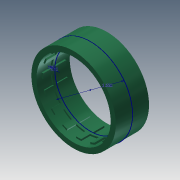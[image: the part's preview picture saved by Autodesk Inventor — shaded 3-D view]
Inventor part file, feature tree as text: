
AUTODESK INVENTOR PART (.ipt)
format: ipt  version: 2015 (Build 190159000, 159)  size: 231,424 bytes
history: native  units: in
note: dims shown in document units (in); Inventor stores cm internally (conversion verified against a paired STEP export)
features: extrude x3, sketch x2, plane x1, pattern_circular x1
ambient origin geometry x8: Origin, YZ Plane, XZ Plane, XY Plane, X Axis, Y Axis, Z Axis, Center Point
bodies: Body1 (feature_tree)
feature tree (7):
  sketch  "Sketch2"  dims[d4=1.65in d5=0.1in]
  extrude  "Extrusion2"  Depth=0.1in
  plane  "Work Plane1"
  extrude  "Extrusion3"  Depth=0.65in TaperAngle=0.0deg
  pattern_circular  "Circular Pattern1"  [2 undecoded]
  extrude  "Extrusion4"  Depth=0.05in
  sketch  "Sketch4"  dims[d6=0.03in d7=0.65in d8=0.0in d11=0.0275in d12=0.0275in d13=0.45in d14=0.0in d15=6.2992in d16=360.0deg d18=0.05in d19=0.0in]
note: 2 required parameter values undecoded (feature->parameter linkage not recoverable at this tier; creation-order binding heuristic only, values carry confidence <= 0.55)
